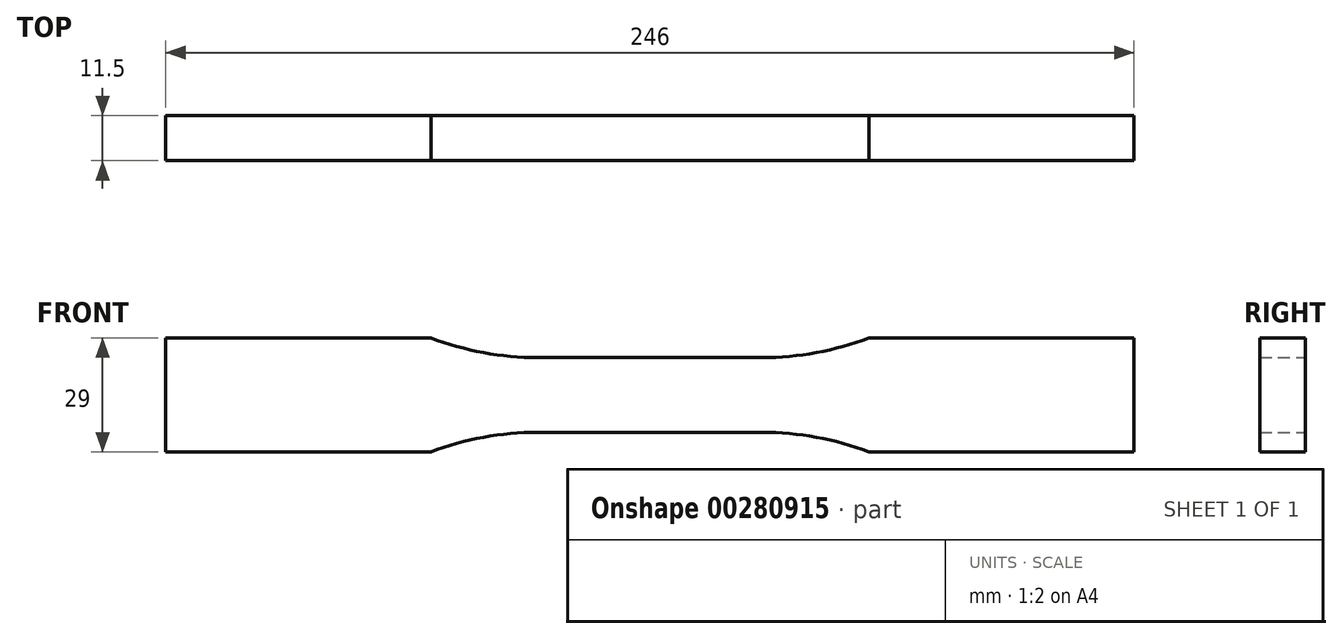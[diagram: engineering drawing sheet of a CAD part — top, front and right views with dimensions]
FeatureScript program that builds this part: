
annotation { "Feature Type Name" : "Feature", "Feature Type Description" : "" }
export const myFeature = defineFeature(function(context is Context, id is Id, definition is map)
    precondition{}
    {
        {
            var Q0;
            Q0=qCreatedBy(makeId("Front.planeOp"),FACE);
            var sketch = newSketch(context, id + "F0", { "sketchPlane" : qUnion([Q0])});
            skLineSegment(sketch, "E0", {"start": v(0, 9.5) * mm, "end": v(28.5, 9.5) * mm});
            skLineSegment(sketch, "E1", {"start": v(55.65, 14.5) * mm, "end": v(123, 14.5) * mm});
            skLineSegment(sketch, "E2", {"start": v(123, 14.5) * mm, "end": v(123, 0) * mm});
            skArc(sketch, "E3", {"start": v(28.5, 9.5) * mm, "mid": v(42.3, 10.76) * mm, "end": v(55.65, 14.5) * mm});
            skLineSegment(sketch, "E4.MirrorCS", {"start": v(55.65, -14.5) * mm, "end": v(123, -14.5) * mm});
            skArc(sketch, "E5.MirrorCS", {"start": v(28.5, -9.5) * mm, "mid": v(42.3, -10.76) * mm, "end": v(55.65, -14.5) * mm});
            skLineSegment(sketch, "E6.MirrorCS", {"start": v(123, -14.5) * mm, "end": v(123, 0) * mm});
            skLineSegment(sketch, "E7.MirrorCS", {"start": v(0, -9.5) * mm, "end": v(28.5, -9.5) * mm});
            skLineSegment(sketch, "E8.MirrorCS", {"start": v(0, -9.5) * mm, "end": v(-28.5, -9.5) * mm});
            skLineSegment(sketch, "E9.MirrorCS", {"start": v(-123, -14.5) * mm, "end": v(-123, 0) * mm});
            skLineSegment(sketch, "E10.MirrorCS", {"start": v(0, 9.5) * mm, "end": v(-28.5, 9.5) * mm});
            skLineSegment(sketch, "E11.MirrorCS", {"start": v(-55.65, 14.5) * mm, "end": v(-123, 14.5) * mm});
            skLineSegment(sketch, "E12.MirrorCS", {"start": v(-123, 14.5) * mm, "end": v(-123, 0) * mm});
            skArc(sketch, "E13.MirrorCS", {"start": v(-28.5, -9.5) * mm, "mid": v(-42.3, -10.76) * mm, "end": v(-55.65, -14.5) * mm});
            skLineSegment(sketch, "E14.MirrorCS", {"start": v(-55.65, -14.5) * mm, "end": v(-123, -14.5) * mm});
            skArc(sketch, "E15.MirrorCS", {"start": v(-28.5, 9.5) * mm, "mid": v(-42.3, 10.76) * mm, "end": v(-55.65, 14.5) * mm});
            skSolve(sketch);
        }
        {
            var Q0;
            Q0=makeQuery(id+"F0.imprint","IMPRINT",FACE,{"disambiguationData":[TD([[makeQuery(id+"F0.imprint","IMPRINT",EDGE,{"derivedFrom":sQuery(id+"F0.wireOp",EDGE,"E0")}),-1.0]])]});
            extrude(context, id + "F1", {"entities" : qUnion([Q0]), "depth" : 11.5 * mm});
        }
    });
